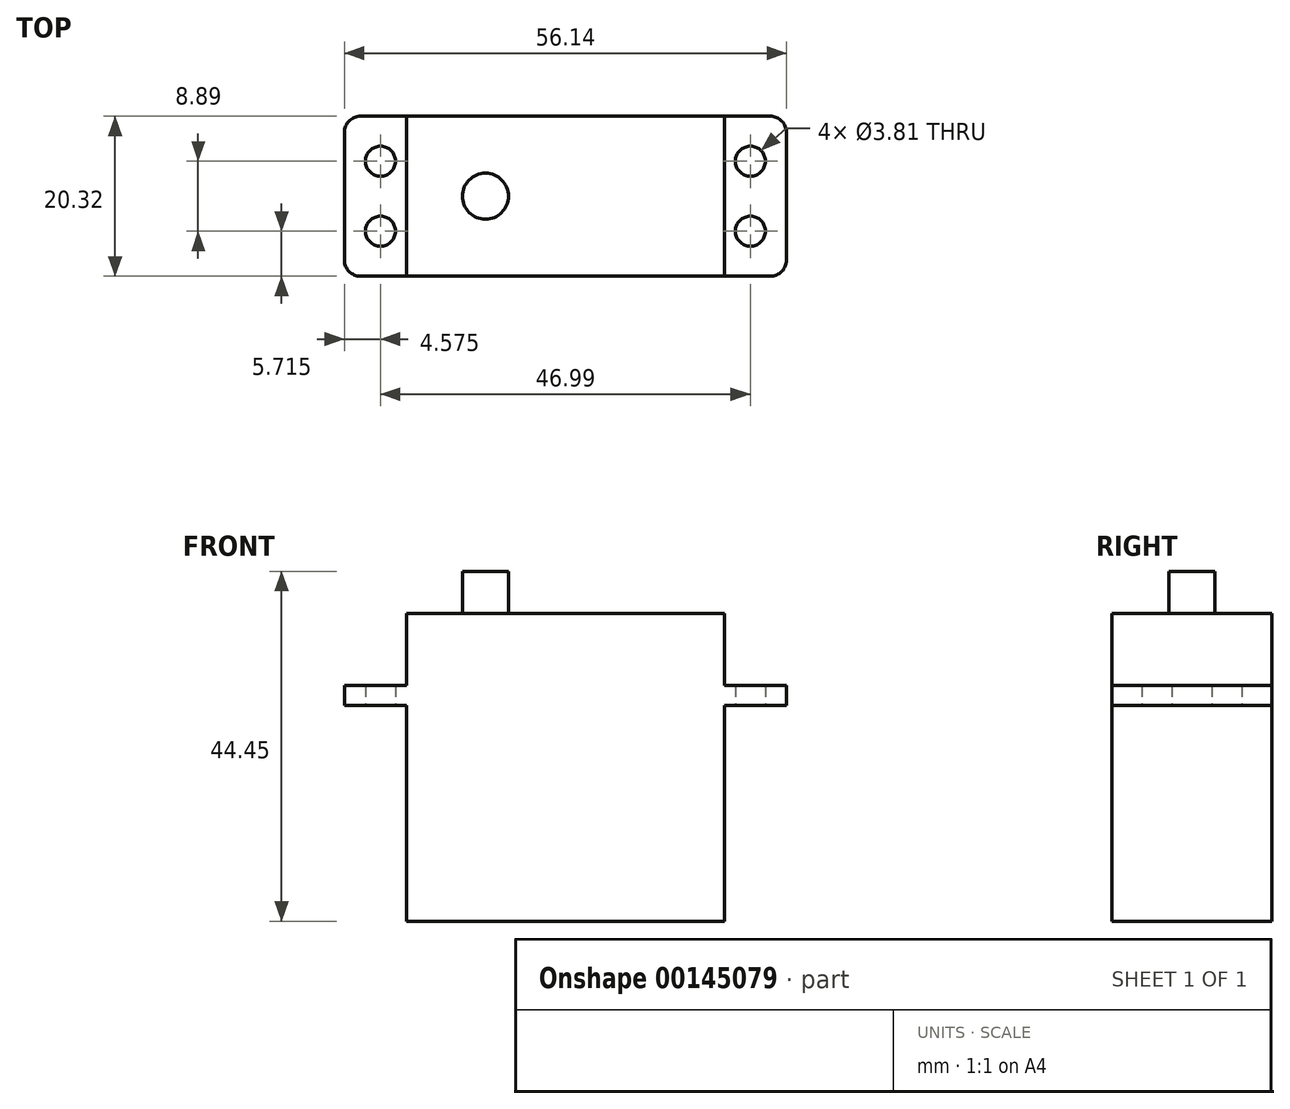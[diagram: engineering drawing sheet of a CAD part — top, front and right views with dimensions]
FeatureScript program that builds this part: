
annotation { "Feature Type Name" : "Feature", "Feature Type Description" : "" }
export const myFeature = defineFeature(function(context is Context, id is Id, definition is map)
    precondition{}
    {
        {
            var Q0;
            Q0=qCreatedBy(makeId("Top.planeOp"),FACE);
            var sketch = newSketch(context, id + "F0", { "sketchPlane" : qUnion([Q0])});
            skLineSegment(sketch, "E0.bottom", {"start": v(-20.2, 10.16) * mm, "end": v(20.2, 10.16) * mm});
            skLineSegment(sketch, "E0.top", {"start": v(-20.2, -10.16) * mm, "end": v(20.2, -10.16) * mm});
            skLineSegment(sketch, "E0.left", {"start": v(-20.2, 10.16) * mm, "end": v(-20.2, -10.16) * mm});
            skLineSegment(sketch, "E0.right", {"start": v(20.2, 10.16) * mm, "end": v(20.2, -10.16) * mm});
            skSolve(sketch);
        }
        {
            var Q0;
            Q0 = qSketchRegion(id + "F0", true);
            extrude(context, id + "F1", {"entities" : qUnion([Q0]), "oppositeDirection" : true, "depth" : 27.43 * mm, "hasSecondDirection" : true, "secondDirectionOppositeDirection" : false, "secondDirectionDepth" : 11.68 * mm});
        }
        {
            var Q0;
            Q0=qCreatedBy(makeId("Top.planeOp"),FACE);
            var sketch = newSketch(context, id + "F2", { "sketchPlane" : qUnion([Q0])});
            skLineSegment(sketch, "E1.bottom", {"start": v(-26.04, 10.16) * mm, "end": v(26.04, 10.16) * mm});
            skLineSegment(sketch, "E1.top", {"start": v(-26.04, -10.16) * mm, "end": v(26.04, -10.16) * mm});
            skLineSegment(sketch, "E1.left", {"start": v(-28.07, 8.13) * mm, "end": v(-28.07, -8.13) * mm});
            skLineSegment(sketch, "E1.right", {"start": v(28.07, 8.13) * mm, "end": v(28.07, -8.13) * mm});
            skPoint(sketch, "E2.visualSharp", {"position": v(-28.07, 10.16) * mm});
            skArc(sketch, "E2.filletArc", {"start": v(-26.04, 10.16) * mm, "mid": v(-27.47, 9.56) * mm, "end": v(-28.07, 8.13) * mm});
            skPoint(sketch, "E3.visualSharp", {"position": v(-28.07, -10.16) * mm});
            skArc(sketch, "E3.filletArc", {"start": v(-28.07, -8.13) * mm, "mid": v(-27.47, -9.56) * mm, "end": v(-26.04, -10.16) * mm});
            skPoint(sketch, "E4.visualSharp", {"position": v(28.07, -10.16) * mm});
            skArc(sketch, "E4.filletArc", {"start": v(26.04, -10.16) * mm, "mid": v(27.47, -9.56) * mm, "end": v(28.07, -8.13) * mm});
            skPoint(sketch, "E5.visualSharp", {"position": v(28.07, 10.16) * mm});
            skArc(sketch, "E5.filletArc", {"start": v(28.07, 8.13) * mm, "mid": v(27.47, 9.56) * mm, "end": v(26.04, 10.16) * mm});
            skLineSegment(sketch, "E6.bottom", {"start": v(-23.5, 4.45) * mm, "end": v(23.5, 4.44) * mm, "construction": true});
            skLineSegment(sketch, "E6.top", {"start": v(-23.5, -4.44) * mm, "end": v(23.5, -4.45) * mm, "construction": true});
            skLineSegment(sketch, "E6.left", {"start": v(-23.5, 4.44) * mm, "end": v(-23.5, -4.44) * mm, "construction": true});
            skLineSegment(sketch, "E6.right", {"start": v(23.5, 4.44) * mm, "end": v(23.5, -4.44) * mm, "construction": true});
            skCircle(sketch, "E7", {"center": v(-23.5, 4.45) * mm, "radius": 1.9 * mm});
            skCircle(sketch, "E8", {"center": v(-23.5, -4.44) * mm, "radius": 1.9 * mm});
            skCircle(sketch, "E9", {"center": v(23.5, -4.45) * mm, "radius": 1.9 * mm});
            skCircle(sketch, "E10", {"center": v(23.5, 4.44) * mm, "radius": 1.9 * mm});
            skSolve(sketch);
        }
        {
            var Q0;
            Q0 = qSketchRegion(id + "F2", true);
            extrude(context, id + "F3", {"entities" : qUnion([Q0]), "operationType" : NewBodyOperationType.ADD, "depth" : 2.54 * mm});
        }
        {
            var Q0;
            Q0=makeQuery(id+"F1.opExtrude","CAP_FACE",FACE,{"disambiguationData":[OSD([sQuery(id+"F0.wireOp",EDGE,"E0.bottom"),sQuery(id+"F0.wireOp",EDGE,"E0.top"),sQuery(id+"F0.wireOp",EDGE,"E0.left"),sQuery(id+"F0.wireOp",EDGE,"E0.right")])],"isStart":true});
            var sketch = newSketch(context, id + "F4", { "sketchPlane" : qUnion([Q0])});
            skCircle(sketch, "E11", {"center": v(-10.16, 0) * mm, "radius": 2.92 * mm});
            skSolve(sketch);
        }
        {
            var Q0;
            Q0 = qSketchRegion(id + "F4", true);
            extrude(context, id + "F5", {"entities" : qUnion([Q0]), "operationType" : NewBodyOperationType.ADD, "depth" : 5.33 * mm});
        }
    });
